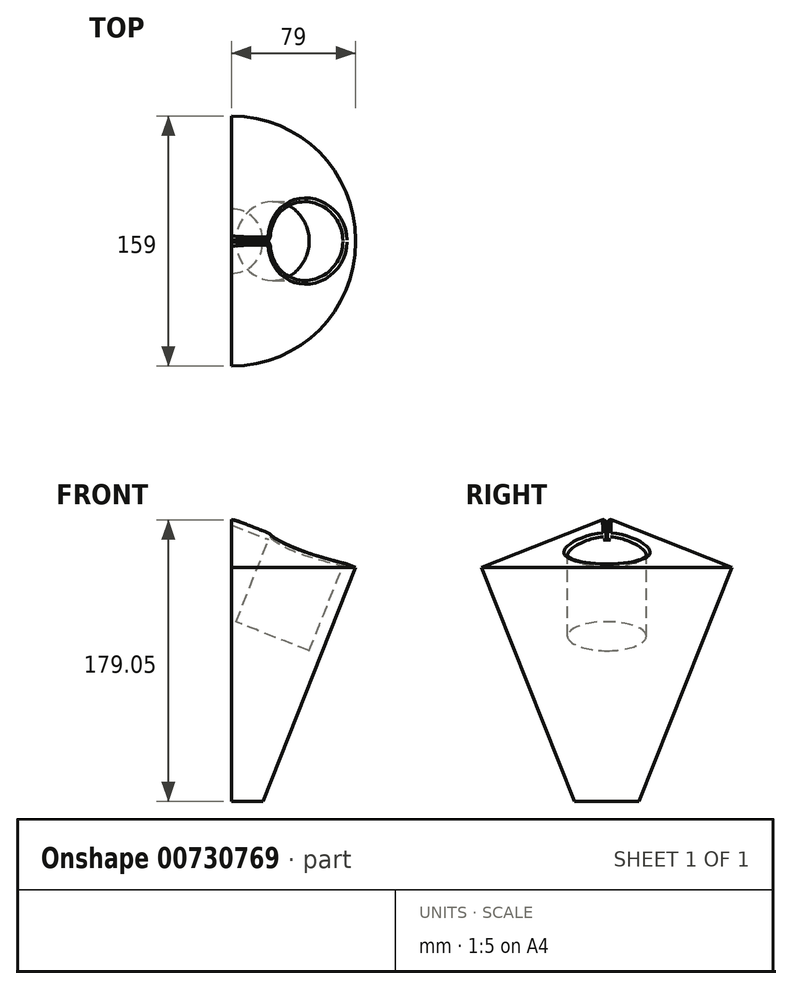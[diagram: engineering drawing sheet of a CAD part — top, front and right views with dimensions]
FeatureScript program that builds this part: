
annotation { "Feature Type Name" : "Feature", "Feature Type Description" : "" }
export const myFeature = defineFeature(function(context is Context, id is Id, definition is map)
    precondition{}
    {
        {
            var Q0;
            Q0=qCreatedBy(makeId("Front.planeOp"),FACE);
            var sketch = newSketch(context, id + "F0", { "sketchPlane" : qUnion([Q0])});
            skLineSegment(sketch, "E0", {"start": v(0, 0) * mm, "end": v(0, 180) * mm});
            skLineSegment(sketch, "E1", {"start": v(0, 180) * mm, "end": v(79, 148.64) * mm});
            skLineSegment(sketch, "E2", {"start": v(79, 148.64) * mm, "end": v(20, 0) * mm});
            skLineSegment(sketch, "E3", {"start": v(20, 0) * mm, "end": v(0, 0) * mm});
            skSolve(sketch);
        }
        {
            var Q0;
            Q0=makeQuery(id+"F0.imprint","IMPRINT",FACE,{"disambiguationData":[TD([[makeQuery(id+"F0.imprint","IMPRINT",EDGE,{"derivedFrom":sQuery(id+"F0.wireOp",EDGE,"E0")}),-1.0]])]});
            extrude(context, id + "F1", {"entities" : qUnion([Q0]), "endBound" : BoundingType.SYMMETRIC, "depth" : 1 * mm, "offsetDistance" : 25 * mm});
        }
        {
            var Q0;
            Q0=makeQuery(id+"F1.opExtrude","CAP_FACE",FACE,{"disambiguationData":[OSD([sQuery(id+"F0.wireOp",EDGE,"E0"),sQuery(id+"F0.wireOp",EDGE,"E1"),sQuery(id+"F0.wireOp",EDGE,"E2"),sQuery(id+"F0.wireOp",EDGE,"E3")])],"isStart":false});
            var Q1;
            Q1=makeQuery(id+"F1.opExtrude","CAP_EDGE",EDGE,{"disambiguationData":[OSD([sQuery(id+"F0.wireOp",EDGE,"E0")])],"isStart":false});
            revolve(context, id + "F2", {"operationType" : NewBodyOperationType.ADD, "surfaceOperationType" : NewSurfaceOperationType.NEW, "entities" : qUnion([Q0]), "axis" : qUnion([Q1]), "revolveType" : RevolveType.ONE_DIRECTION, "oppositeDirection" : true, "angle" : 90 * degree});
        }
        {
            var Q0;
            Q0=makeQuery(id+"F1.opExtrude","CAP_FACE",FACE,{"disambiguationData":[OSD([sQuery(id+"F0.wireOp",EDGE,"E0"),sQuery(id+"F0.wireOp",EDGE,"E1"),sQuery(id+"F0.wireOp",EDGE,"E2"),sQuery(id+"F0.wireOp",EDGE,"E3")])],"isStart":true});
            var Q1;
            Q1=makeQuery(id+"F1.opExtrude","CAP_EDGE",EDGE,{"disambiguationData":[OSD([sQuery(id+"F0.wireOp",EDGE,"E0")])],"isStart":true});
            revolve(context, id + "F3", {"operationType" : NewBodyOperationType.ADD, "surfaceOperationType" : NewSurfaceOperationType.NEW, "entities" : qUnion([Q0]), "axis" : qUnion([Q1]), "revolveType" : RevolveType.ONE_DIRECTION, "angle" : 90 * degree});
        }
        {
            var Q0;
            Q0=makeQuery(id+"F1.opExtrude","SWEPT_FACE",FACE,{"disambiguationData":[OSD([sQuery(id+"F0.wireOp",EDGE,"E1")])]});
            var sketch = newSketch(context, id + "F4", { "sketchPlane" : qUnion([Q0])});
            skLineSegment(sketch, "E4", {"start": v(-66.41, -0.5) * mm, "end": v(18.59, 0.5) * mm, "construction": true});
            skCircle(sketch, "E5", {"center": v(-14.41, 0) * mm, "radius": 25 * mm});
            skLineSegment(sketch, "E6", {"start": v(18.59, 0) * mm, "end": v(-66.41, 0) * mm, "construction": true});
            skSolve(sketch);
        }
        {
            var Q0;
            {var subQ0=sQuery(id+"F4.wireOp",EDGE,"E5");var subQ1=sQuery(id+"F0.wireOp",EDGE,"E1");var subQ2=makeQuery(id+"F3.boolean.opBoolean","MERGE",EDGE,{"derivedFrom":[makeQuery(id+"F1.opExtrude","CAP_EDGE",EDGE,{"disambiguationData":[OSD([subQ1])],"isStart":true}),makeQuery(id+"F3.opRevolve","CAP_EDGE",EDGE,{"disambiguationData":[OSD([subQ1])],"isStart":true})]});var subQ3=makeQuery(id+"F4.imprint","INTERSECT",VERTEX,{"disambiguationData":[OD(0.0)],"derivedFrom":[subQ2,subQ0]});Q0=makeQuery(id+"F4.imprint","IMPRINT",FACE,{"disambiguationData":[TD([[makeQuery(id+"F4.imprint","IMPRINT",EDGE,{"disambiguationData":[TD([[subQ3,1.0]])],"derivedFrom":subQ0}),1.0]])]});}
            var Q1;
            {var subQ0=sQuery(id+"F4.wireOp",EDGE,"E5");var subQ1=sQuery(id+"F0.wireOp",EDGE,"E1");var subQ2=makeQuery(id+"F3.boolean.opBoolean","MERGE",EDGE,{"derivedFrom":[makeQuery(id+"F1.opExtrude","CAP_EDGE",EDGE,{"disambiguationData":[OSD([subQ1])],"isStart":true}),makeQuery(id+"F3.opRevolve","CAP_EDGE",EDGE,{"disambiguationData":[OSD([subQ1])],"isStart":true})]});var subQ3=makeQuery(id+"F4.imprint","INTERSECT",VERTEX,{"disambiguationData":[OD(0.0)],"derivedFrom":[subQ2,subQ0]});Q1=makeQuery(id+"F4.imprint","IMPRINT",FACE,{"disambiguationData":[TD([[makeQuery(id+"F4.imprint","IMPRINT",EDGE,{"disambiguationData":[TD([[subQ3,-1.0]])],"derivedFrom":subQ0}),1.0]])]});}
            var Q2;
            {var subQ0=sQuery(id+"F4.wireOp",EDGE,"E5");var subQ1=sQuery(id+"F0.wireOp",EDGE,"E1");var subQ2=makeQuery(id+"F2.boolean.opBoolean","MERGE",EDGE,{"derivedFrom":[makeQuery(id+"F1.opExtrude","CAP_EDGE",EDGE,{"disambiguationData":[OSD([subQ1])],"isStart":false}),makeQuery(id+"F2.opRevolve","CAP_EDGE",EDGE,{"disambiguationData":[OSD([subQ1])],"isStart":true})]});var subQ3=makeQuery(id+"F4.imprint","INTERSECT",VERTEX,{"disambiguationData":[OD(0.0)],"derivedFrom":[subQ2,subQ0]});Q2=makeQuery(id+"F4.imprint","IMPRINT",FACE,{"disambiguationData":[TD([[makeQuery(id+"F4.imprint","IMPRINT",EDGE,{"disambiguationData":[TD([[subQ3,-1.0]])],"derivedFrom":subQ0}),1.0]])]});}
            extrude(context, id + "F5", {"entities" : qUnion([Q0, Q1, Q2]), "operationType" : NewBodyOperationType.REMOVE, "oppositeDirection" : true, "depth" : 60 * mm, "offsetDistance" : 25 * mm});
        }
        {
            var Q0;
            {var subQ0=sQuery(id+"F0.wireOp",EDGE,"E1");var subQ3=sQuery(id+"F0.wireOp",EDGE,"E0");Q0=makeQuery(id+"F5.boolean.opBoolean","SPLIT",FACE,{"disambiguationData":[TD([makeQuery(id+"F1.opExtrude","SWEPT_FACE",FACE,{"disambiguationData":[OSD([subQ3])]})])],"derivedFrom":makeQuery(id+"F1.opExtrude","SWEPT_FACE",FACE,{"disambiguationData":[OSD([subQ0])]})});}
            extrude(context, id + "F6", {"entities" : qUnion([Q0]), "operationType" : NewBodyOperationType.REMOVE, "oppositeDirection" : true, "depth" : 4 * mm, "offsetDistance" : 25 * mm});
        }
        {
            var Q0;
            Q0=makeQuery(id+"F5.boolean.opBoolean","INTERSECT",EDGE,{"derivedFrom":[makeQuery(id+"F2.opRevolve","SWEPT_FACE",FACE,{"disambiguationData":[OSD([sQuery(id+"F0.wireOp",EDGE,"E1")])]}),makeQuery(id+"F5.opExtrude","SWEPT_FACE",FACE,{"disambiguationData":[OSD([sQuery(id+"F4.wireOp",EDGE,"E5")])]})]});
            var Q1;
            Q1=makeQuery(id+"F5.boolean.opBoolean","INTERSECT",EDGE,{"derivedFrom":[makeQuery(id+"F3.opRevolve","SWEPT_FACE",FACE,{"disambiguationData":[OSD([sQuery(id+"F0.wireOp",EDGE,"E1")])]}),makeQuery(id+"F5.opExtrude","SWEPT_FACE",FACE,{"disambiguationData":[OSD([sQuery(id+"F4.wireOp",EDGE,"E5")])]})]});
            var Q2;
            Q2=makeQuery(id+"F5.boolean.opBoolean","COPY",EDGE,{"disambiguationData":[OD(1.0)],"derivedFrom":makeQuery(id+"F5.opExtrude","CAP_EDGE",EDGE,{"disambiguationData":[OSD([sQuery(id+"F4.wireOp",EDGE,"E5")])],"isStart":true})});
            fillet(context, id + "F7", {"entities" : qUnion([Q0, Q1, Q2]), "radius" : 2 * mm, "tangentPropagation" : true, "allowEdgeOverflow" : false});
        }
        {
            var Q0;
            {var subQ0=sQuery(id+"F0.wireOp",EDGE,"E1");var subQ3=sQuery(id+"F0.wireOp",EDGE,"E0");var subQ4=makeQuery(id+"F5.boolean.opBoolean","SPLIT",EDGE,{"disambiguationData":[TD([makeQuery(id+"F1.opExtrude","SWEPT_FACE",FACE,{"disambiguationData":[OSD([subQ3])]})])],"derivedFrom":makeQuery(id+"F2.boolean.opBoolean","MERGE",EDGE,{"derivedFrom":[makeQuery(id+"F1.opExtrude","CAP_EDGE",EDGE,{"disambiguationData":[OSD([subQ0])],"isStart":false}),makeQuery(id+"F2.opRevolve","CAP_EDGE",EDGE,{"disambiguationData":[OSD([subQ0])],"isStart":true})]})});Q0=makeQuery(id+"F6.boolean.opBoolean","MERGE",EDGE,{"derivedFrom":[subQ4,makeQuery(id+"F6.opExtrude","CAP_EDGE",EDGE,{"disambiguationData":[OSD([subQ0]),TDD([subQ4])],"isStart":true})]});}
            var Q1;
            {var subQ0=sQuery(id+"F0.wireOp",EDGE,"E1");var subQ3=sQuery(id+"F0.wireOp",EDGE,"E0");var subQ4=makeQuery(id+"F5.boolean.opBoolean","SPLIT",EDGE,{"disambiguationData":[TD([makeQuery(id+"F1.opExtrude","SWEPT_FACE",FACE,{"disambiguationData":[OSD([subQ3])]})])],"derivedFrom":makeQuery(id+"F3.boolean.opBoolean","MERGE",EDGE,{"derivedFrom":[makeQuery(id+"F1.opExtrude","CAP_EDGE",EDGE,{"disambiguationData":[OSD([subQ0])],"isStart":true}),makeQuery(id+"F3.opRevolve","CAP_EDGE",EDGE,{"disambiguationData":[OSD([subQ0])],"isStart":true})]})});Q1=makeQuery(id+"F6.boolean.opBoolean","MERGE",EDGE,{"derivedFrom":[subQ4,makeQuery(id+"F6.opExtrude","CAP_EDGE",EDGE,{"disambiguationData":[OSD([subQ0]),TDD([subQ4])],"isStart":true})]});}
            fillet(context, id + "F8", {"entities" : qUnion([Q0, Q1]), "radius" : 2 * mm, "tangentPropagation" : true, "allowEdgeOverflow" : false});
        }
    });
